# Revit family: DIN-Kreuzverbinder für Flachleiter, mit Zwischenplatte
name_source: partatom
category: Generic Models
revit_build: Autodesk Revit 2015 (Build: 20140606_1530(x64)
units: mm (PartAtom-declared; Revit-internal decimal feet)

## types (2) — shared parameters
Height = 3 mm  [stored 0.00984252 ft]
Height 1 = 6 mm  [stored 0.019685 ft]
Manufacturer = OBO Bettermann
Material = Hot-dip galvanised
URL = http://www.obo-bettermann.com

## per-type parameters (varying)
| type | GTIN | Length | Length 1 | Length 2 | Manufacturer Art.No. | Width | Width 1 | Width 2 |
| 256 DIN 30 FT | 4012195419297 | 60 mm  [stored 0.19685 ft] | 20 mm  [stored 0.0656168 ft] | 14 mm  [stored 0.0459318 ft] | 5314615 | 60 mm  [stored 0.19685 ft] | 20 mm  [stored 0.0656168 ft] | 13 mm |
| 256 DIN 40 FT | 4012195419358 | 80 mm  [stored 0.262467 ft] | 27 mm  [stored 0.0885827 ft] | 21 mm | 5314623 | 80 mm  [stored 0.262467 ft] | 27 mm  [stored 0.0885827 ft] | 20 mm  [stored 0.0656168 ft] |

note: column(s) folded — value = type name in every type: Article Type

note: [stored X ft] marks values corroborated as IEEE doubles in the binary element streams (Revit-internal decimal feet)

## geometry (parser evidence)
native form markers: Sweep x2
no freeform markers — native parametric forms only
